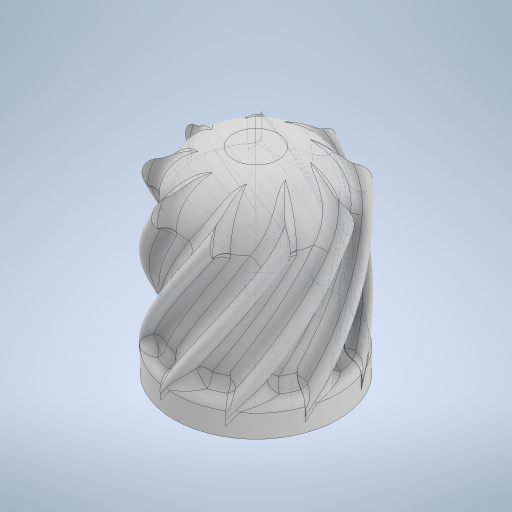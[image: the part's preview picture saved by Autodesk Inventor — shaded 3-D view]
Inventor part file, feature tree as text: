
AUTODESK INVENTOR PART (.ipt)
format: ipt  version: 2023 (Build 270158030, 158C)  size: 1,700,352 bytes
history: native  units: mm
features: fillet x4, sketch x4, projected_geometry x4, extrude x3, helix x1, pattern_circular x1
ambient origin geometry x8: Origin, YZ Plane, XZ Plane, XY Plane, X Axis, Y Axis, Z Axis, Center Point
bodies: Solid1 (feature_tree)
feature tree (17):
  extrude  "Extrusion1"  Depth=16.5mm TaperAngle=0.0deg
  extrude  "Extrusion2"  Depth=7.1mm
  extrude  "Extrusion3"  Depth=3.55mm
  fillet  "Fillet1"  Radius=13.2mm
  helix  "Coil1"  [1 undecoded]
  fillet  "Fillet3"  Radius=13.8mm
  fillet  "Fillet2"  Radius=2.4mm
  pattern_circular  "Circular Pattern1"  [2 undecoded]
  fillet  "Fillet4"  Radius=1.0mm
  sketch  "Sketch1"  dims[d0=13.85mm d1=16.5mm d2=0.0mm]
  sketch  "Sketch2"  dims[d3=7.1mm d4=7.1mm]
  sketch  "Sketch3"  dims[d5=3.55mm d6=3.55mm d7=13.2mm d8=0.0mm d9=11.6mm d10=13.8mm d11=0.0mm d12=2.4mm]
  projected_geometry  "Projected Loop1"
  sketch  "Sketch4"  dims[d13=1.2mm d14=70.0mm d15=12.0mm d16=2.0mm d17=0.0mm d18=90.0deg d19=90.0deg d20=0.0mm d21=0.174533mm d22=3.9mm d23=0.9mm d24=1.0mm d25=0.1mm d26=90.0mm d27=360.0deg]
  projected_geometry  "Projected Loop2"
  projected_geometry  "Projected Loop3"
  projected_geometry  "Projected Loop4"
note: 3 required parameter values undecoded (feature->parameter linkage not recoverable at this tier; creation-order binding heuristic only, values carry confidence <= 0.55)
